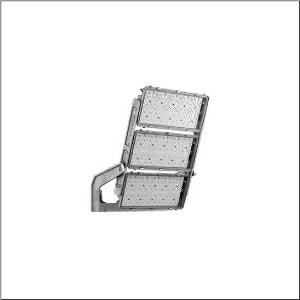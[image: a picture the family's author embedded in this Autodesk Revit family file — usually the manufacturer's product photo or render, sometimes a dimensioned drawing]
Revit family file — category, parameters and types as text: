
# Revit family: floodlight_fl_11_maxi_pro_remote___pl52_5xa779426d01aa_14f9
name_source: partatom
category: Lighting Fixtures
units: mm (PartAtom-declared; Revit-internal decimal feet)

## family parameters
Cut with Voids When Loaded = No
Host = Face
Light Source = No
Part Type = Normal
Room Calculation Point = No
Round Connector Dimension = Use Diameter
Shared = No

## types (1)
- --- (1 x LED, 169140 lm, 1387.6 W, 4000K)
    Apparent Load = 1388 VA
    CIE Flux Codes = 24 55 98 100 100
    Color Rendering = 70
    Color Temperature = 4000K
    Default Elevation = 1800 mm
    Description = Floodlight FL 11  maxi  pro Remote floodlight; light control with lens of PMMA; cover panel of toughened safety glass, transparent; light distribution: PL52, asymmetric direct distribution, LEDcolour temperature: 4000K, rated luminous flux: 169.140lm, colour rendering: CRI > 70, light colour: 740; luminous efficacy: 122lm/W; brightness control: DALI 2 (1 DALI address); with terminal, 8-pole, max. 2.5mm², mains connection: 220..240V/380..400V AC, 50/60Hz, surge voltage resistance: line to ground: 10kV, ECG replaceable separately, LED unit replaceable without ESD environment, dustproof LED module, dimming range 10..100%, no afterglow with DALI off / DMX off command; 1388W floodlight with 3x LED unit of diecast aluminium, coated grey; length: 713mm / width: 651mm / height: 338mm; mounting bracket, of diecast aluminium, uncoated, natural, equipment: Power, protection rating (complete): IP66; insulation class (complete): insulation class I (protective earthing); certification: CE, ENEC, VDE; ball protection: ball impact resistance with accessories, rated ambient temperature 10°C, only for outdoor installations, permissible operating ambient temperature: -40..+30°C, permissible storage temperature: -40..+85°C; packaging unit: 1 piece

Light Distribution: PL52
    Height = 320 mm
    Lamp = 1 x LED
    Lamp Light Flux = 169140 lm
    Lamp Power = 1387.6 W
    Lamp count = 1
    Length = 1002 mm
    Luminous efficacy = 122 lm/W
    Manufacturer = Siteco
    ModVariant = No
    Model = 5XA779426D01AA
    Number of Poles = 1
    OnlyDefault = Yes
    Power Factor = 1
    Product Name = Floodlight FL 11 maxi pro Remote | PL52
    Product group = floodlight | pylon top
    ProductGroupID = 6101
    Protection Class = Protection class I
    Protection Degree = IP 66
    RLX_Detail_Level = 1
    RlxData = <blob elided: 52485 chars, md5=333ae98f>
    Socket = socket
    Standby Power = 0 W
    System Light Flux = 169140 lm
    System Power = 1388 W
    Type Comments = factory setting: luminous flux: 100 % | dim-lin: 254 | 955 mA
    Type Image = l_1006784.jpg
    URL = http://relux.com
    VarID = @adj_007463
    Voltage = 0 V
    Weight = 0.00 kg
    Width = 655 mm

## geometry (parser evidence)
native form markers: Blend x4, Sweep x14
no freeform markers — native parametric forms only
